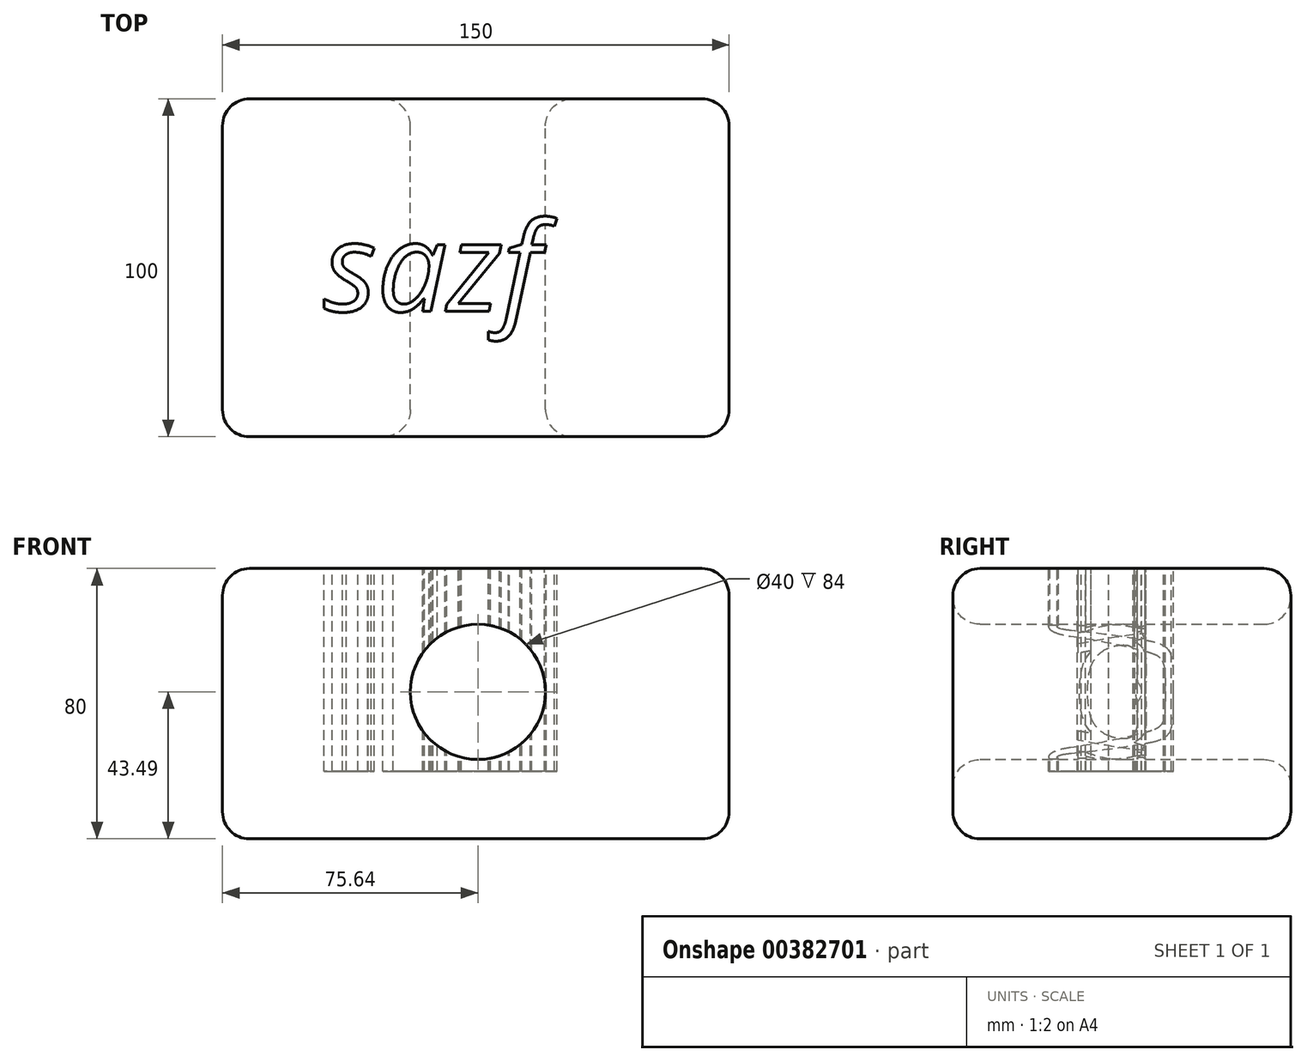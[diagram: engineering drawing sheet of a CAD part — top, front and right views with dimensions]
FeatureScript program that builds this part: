
annotation { "Feature Type Name" : "Feature", "Feature Type Description" : "" }
export const myFeature = defineFeature(function(context is Context, id is Id, definition is map)
    precondition{}
    {
        {
            var Q0;
            Q0=qCreatedBy(makeId("Front.planeOp"),FACE);
            var sketch = newSketch(context, id + "F0", { "sketchPlane" : qUnion([Q0])});
            skLineSegment(sketch, "E0.bottom", {"start": v(-75.64, 36.5) * mm, "end": v(74.36, 36.5) * mm});
            skLineSegment(sketch, "E0.top", {"start": v(-75.64, -43.5) * mm, "end": v(74.36, -43.5) * mm});
            skLineSegment(sketch, "E0.left", {"start": v(-75.64, 36.5) * mm, "end": v(-75.64, -43.5) * mm});
            skLineSegment(sketch, "E0.right", {"start": v(74.36, 36.5) * mm, "end": v(74.36, -43.5) * mm});
            skCircle(sketch, "E1", {"center": v(0, 0) * mm, "radius": 20 * mm});
            skSolve(sketch);
        }
        {
            var Q0;
            Q0 = qSketchRegion(id + "F0", true);
            extrude(context, id + "F1", {"entities" : qUnion([Q0]), "endBound" : BoundingType.SYMMETRIC, "depth" : 100 * mm});
        }
        {
            var Q0;
            Q0=makeQuery(id+"F1.opExtrude","SWEPT_FACE",FACE,{"disambiguationData":[OSD([sQuery(id+"F0.wireOp",EDGE,"E0.bottom")])]});
            var sketch = newSketch(context, id + "F2", { "sketchPlane" : qUnion([Q0])});
            skText(sketch, "E2", { "text": "sazf", "fontName": "OpenSans-Italic.ttf"});
            const initialGuessF2  = {"E2": [-0.04568, -0.01288, 1, 0, 0.0265]};
            skSetInitialGuess(sketch, initialGuessF2);
            skSolve(sketch);
        }
        {
            var Q0;
            Q0 = qSketchRegion(id + "F2", true);
            extrude(context, id + "F3", {"entities" : qUnion([Q0]), "operationType" : NewBodyOperationType.REMOVE, "oppositeDirection" : true, "depth" : 60 * mm});
        }
        {
            var Q0;
            Q0=makeQuery(id+"F1.opExtrude","CAP_FACE",FACE,{"disambiguationData":[OSD([sQuery(id+"F0.wireOp",EDGE,"E0.bottom"),sQuery(id+"F0.wireOp",EDGE,"E0.top"),sQuery(id+"F0.wireOp",EDGE,"E0.left"),sQuery(id+"F0.wireOp",EDGE,"E0.right"),sQuery(id+"F0.wireOp",EDGE,"E1")])],"isStart":true});
            var Q1;
            Q1=makeQuery(id+"F1.opExtrude","SWEPT_FACE",FACE,{"disambiguationData":[OSD([sQuery(id+"F0.wireOp",EDGE,"E0.right")])]});
            var Q2;
            Q2=makeQuery(id+"F1.opExtrude","CAP_FACE",FACE,{"disambiguationData":[OSD([sQuery(id+"F0.wireOp",EDGE,"E0.bottom"),sQuery(id+"F0.wireOp",EDGE,"E0.top"),sQuery(id+"F0.wireOp",EDGE,"E0.left"),sQuery(id+"F0.wireOp",EDGE,"E0.right"),sQuery(id+"F0.wireOp",EDGE,"E1")])],"isStart":false});
            var Q3;
            Q3=makeQuery(id+"F1.opExtrude","SWEPT_FACE",FACE,{"disambiguationData":[OSD([sQuery(id+"F0.wireOp",EDGE,"E0.left")])]});
            fillet(context, id + "F4", {"entities" : qUnion([Q0, Q1, Q2, Q3]), "radius" : 8 * mm, "tangentPropagation" : true, "allowEdgeOverflow" : false});
        }
    });
